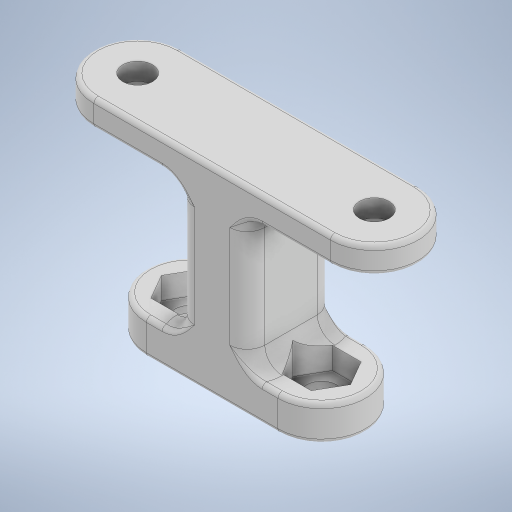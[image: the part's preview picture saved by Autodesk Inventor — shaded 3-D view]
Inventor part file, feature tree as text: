
AUTODESK INVENTOR PART (.ipt)
format: ipt  version: 2024.2 (Build 282272000, 272)  size: 421,888 bytes
history: native  units: mm
features: extrude x6, sketch x6, fillet x2
ambient origin geometry x8: Origin, YZ Plane, XZ Plane, XY Plane, X Axis, Y Axis, Z Axis, Center Point
bodies: Solid1 (feature_tree)
feature tree (14):
  extrude  "Extrusion1"  Depth=27.0mm
  extrude  "Extrusion2"  Depth=10.0mm TaperAngle=0.0deg
  extrude  "Extrusion3"  Depth=15.0mm
  extrude  "Extrusion4"  Depth=5.7mm
  extrude  "Extrusion5"  Depth=3.4mm
  extrude  "Extrusion6"  Depth=0.5mm
  fillet  "Fillet3"  Radius=1.0mm
  fillet  "Fillet2"  Radius=0.5mm
  sketch  "Sketch1"  dims[d0=3.4mm d1=27.0mm]
  sketch  "Sketch2"  dims[d2=10.0mm d3=3.0mm d4=0.0mm]
  sketch  "Sketch3"  dims[d5=15.625mm d6=0.0mm d7=15.0mm]
  sketch  "Sketch4"  dims[d8=4.0mm d9=0.0mm d10=5.7mm]
  sketch  "Sketch5"  dims[d11=2.5mm d12=0.0mm d13=3.4mm]
  sketch  "Sketch6"  dims[d14=2.0mm d15=0.0mm d16=5.1mm d17=1.0mm d18=0.0mm d20=0.5mm d22=8.0mm d23=2.0mm]
